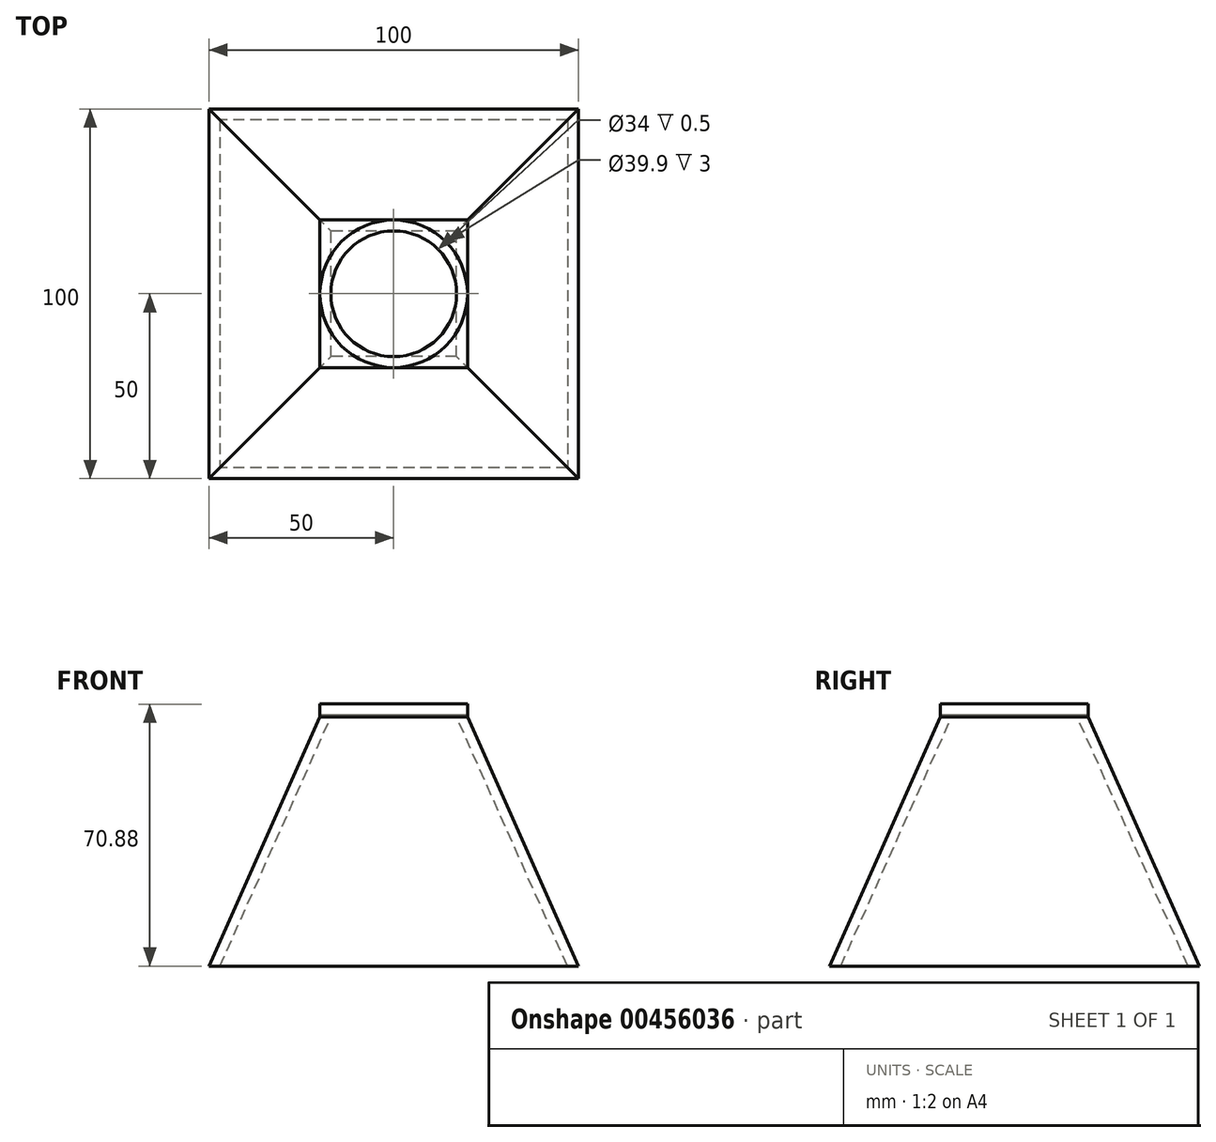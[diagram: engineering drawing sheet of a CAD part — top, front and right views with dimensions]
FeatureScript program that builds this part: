
annotation { "Feature Type Name" : "Feature", "Feature Type Description" : "" }
export const myFeature = defineFeature(function(context is Context, id is Id, definition is map)
    precondition{}
    {
        {
            var Q0;
            Q0=qCreatedBy(makeId("Top.planeOp"),FACE);
            var sketch = newSketch(context, id + "F0", { "sketchPlane" : qUnion([Q0])});
            skLineSegment(sketch, "E0.bottom", {"start": v(50, 50) * mm, "end": v(-50, 50) * mm});
            skLineSegment(sketch, "E0.top", {"start": v(50, -50) * mm, "end": v(-50, -50) * mm});
            skLineSegment(sketch, "E0.left", {"start": v(50, 50) * mm, "end": v(50, -50) * mm});
            skLineSegment(sketch, "E0.right", {"start": v(-50, 50) * mm, "end": v(-50, -50) * mm});
            skPoint(sketch, "E0.middle", {"position": v(0, 0) * mm});
            skLineSegment(sketch, "E1.0", {"start": v(47, -47) * mm, "end": v(-47, -47) * mm, "construction": true});
            skLineSegment(sketch, "E1.1", {"start": v(47, 47) * mm, "end": v(47, -47) * mm, "construction": true});
            skLineSegment(sketch, "E1.2", {"start": v(47, 47) * mm, "end": v(-47, 47) * mm, "construction": true});
            skLineSegment(sketch, "E1.3", {"start": v(-47, 47) * mm, "end": v(-47, -47) * mm, "construction": true});
            skLineSegment(sketch, "E2", {"start": v(0, 50) * mm, "end": v(0, -50) * mm, "construction": true});
            skLineSegment(sketch, "E3", {"start": v(-50, 0) * mm, "end": v(50, 0) * mm, "construction": true});
            skSolve(sketch);
        }
        {
            var Q0;
            Q0=qCreatedBy(makeId("Front.planeOp"),FACE);
            var sketch = newSketch(context, id + "F1", { "sketchPlane" : qUnion([Q0])});
            skLineSegment(sketch, "E4.0", {"start": v(-50, 0) * mm, "end": v(50, 0) * mm, "construction": true});
            skPoint(sketch, "E5.0", {"position": v(47, 0) * mm});
            skLineSegment(sketch, "E6", {"start": v(47, 0) * mm, "end": v(17, 67.38) * mm});
            skPoint(sketch, "E7.0", {"position": v(0, 0) * mm});
            skLineSegment(sketch, "E8", {"start": v(0, 0) * mm, "end": v(0, 105.56) * mm, "construction": true});
            skLineSegment(sketch, "E9", {"start": v(0, 67.38) * mm, "end": v(17, 67.38) * mm, "construction": true});
            skSolve(sketch);
        }
        {
            var Q0;
            Q0=qCreatedBy(makeId("Right.planeOp"),FACE);
            var sketch = newSketch(context, id + "F2", { "sketchPlane" : qUnion([Q0])});
            skLineSegment(sketch, "E10.0", {"start": v(50, 0) * mm, "end": v(-50, 0) * mm, "construction": true});
            skPoint(sketch, "E11.0", {"position": v(47, 0) * mm});
            skLineSegment(sketch, "E12", {"start": v(47, 0) * mm, "end": v(17, 67.38) * mm});
            skLineSegment(sketch, "E13.0", {"start": v(0, 0) * mm, "end": v(0, 105.56) * mm, "construction": true});
            skLineSegment(sketch, "E14", {"start": v(0, 67.38) * mm, "end": v(17, 67.38) * mm, "construction": true});
            skSolve(sketch);
        }
        {
            var Q0;
            Q0=qCreatedBy(makeId("Top.planeOp"),FACE);
            var Q1;
            Q1=sQuery(id+"F1.wireOp",EDGE,"E9");
            cPlane(context, id + "F3", {"entities" : qUnion([Q0, Q1]), "cplaneType" : CPlaneType.LINE_ANGLE, "offset" : 63.5 * mm, "angle" : 0 * degree, "width" : 152.4 * mm, "height" : 152.4 * mm});
        }
        {
            var Q0;
            Q0=qCreatedBy(id+"F3.planeOp",FACE);
            var sketch = newSketch(context, id + "F4", { "sketchPlane" : qUnion([Q0])});
            skCircle(sketch, "E15", {"center": v(0, 0) * mm, "radius": 20 * mm, "construction": true});
            skCircle(sketch, "E16.0", {"center": v(0, 0) * mm, "radius": 17 * mm, "construction": true});
            skLineSegment(sketch, "E17.bottom", {"start": v(20, 20) * mm, "end": v(-20, 20) * mm});
            skLineSegment(sketch, "E17.top", {"start": v(20, -20) * mm, "end": v(-20, -20) * mm});
            skLineSegment(sketch, "E17.left", {"start": v(20, 20) * mm, "end": v(20, -20) * mm});
            skLineSegment(sketch, "E17.right", {"start": v(-20, 20) * mm, "end": v(-20, -20) * mm});
            skPoint(sketch, "E18", {"position": v(0, -20) * mm});
            skPoint(sketch, "E19", {"position": v(20, 0) * mm});
            skLineSegment(sketch, "E20.0", {"start": v(17, -17) * mm, "end": v(-17, -17) * mm, "construction": true});
            skLineSegment(sketch, "E20.1", {"start": v(17, 17) * mm, "end": v(17, -17) * mm, "construction": true});
            skLineSegment(sketch, "E20.2", {"start": v(17, 17) * mm, "end": v(-17, 17) * mm, "construction": true});
            skLineSegment(sketch, "E20.3", {"start": v(-17, 17) * mm, "end": v(-17, -17) * mm, "construction": true});
            skSolve(sketch);
        }
        {
            var Q0;
            Q0=qCreatedBy(makeId("Front.planeOp"),FACE);
            var sketch = newSketch(context, id + "F5", { "sketchPlane" : qUnion([Q0])});
            skPoint(sketch, "E21.1", {"position": v(20, 67.38) * mm});
            skPoint(sketch, "E22.0", {"position": v(50, 0) * mm});
            skLineSegment(sketch, "E23", {"start": v(50, 0) * mm, "end": v(20, 67.38) * mm});
            skSolve(sketch);
        }
        {
            var Q0;
            Q0=qCreatedBy(makeId("Right.planeOp"),FACE);
            var sketch = newSketch(context, id + "F6", { "sketchPlane" : qUnion([Q0])});
            skPoint(sketch, "E24.0", {"position": v(50, 0) * mm});
            skPoint(sketch, "E25.0", {"position": v(20, 67.38) * mm});
            skLineSegment(sketch, "E26", {"start": v(50, 0) * mm, "end": v(20, 67.38) * mm});
            skSolve(sketch);
        }
        {
            var Q0;
            Q0=makeQuery(id+"F0.imprint","IMPRINT",FACE,{"disambiguationData":[TD([[makeQuery(id+"F0.imprint","IMPRINT",EDGE,{"derivedFrom":sQuery(id+"F0.wireOp",EDGE,"E0.bottom")}),1.0]])]});
            var Q1;
            Q1=makeQuery(id+"F4.imprint","IMPRINT",FACE,{"disambiguationData":[TD([[makeQuery(id+"F4.imprint","IMPRINT",EDGE,{"derivedFrom":sQuery(id+"F4.wireOp",EDGE,"E17.bottom")}),1.0]])]});
            var Q2;
            Q2=sQuery(id+"F5.wireOp",EDGE,"E23");
            var Q3;
            Q3=sQuery(id+"F6.wireOp",EDGE,"E26");
            loft(context, id + "F7", {"addGuides" : true, "sheetProfilesArray" : [{ "sheetProfileEntities" : qUnion([Q0]) }, { "sheetProfileEntities" : qUnion([Q1]) }], "guidesArray" : [{ "guideEntities" : qUnion([Q2]), "guideDerivativeType" : LoftGuideDerivativeType.DEFAULT, "guideDerivativeMagnitude" : 1 }, { "guideEntities" : qUnion([Q3]), "guideDerivativeType" : LoftGuideDerivativeType.DEFAULT, "guideDerivativeMagnitude" : 1 }]});
        }
        {
            var Q0;
            Q0=makeQuery(id+"F7.opLoft","CAP_FACE",FACE,{"disambiguationData":[OSD([makeQuery(id+"F0.imprint","IMPRINT",FACE,{"disambiguationData":[TD([[makeQuery(id+"F0.imprint","IMPRINT",EDGE,{"derivedFrom":sQuery(id+"F0.wireOp",EDGE,"E0.bottom")}),1.0]])]})])],"isStart":true});
            var sketch = newSketch(context, id + "F8", { "sketchPlane" : qUnion([Q0])});
            skLineSegment(sketch, "E27.0", {"start": v(47, 47) * mm, "end": v(-47, 47) * mm});
            skLineSegment(sketch, "E27.1", {"start": v(-47, -47) * mm, "end": v(-47, 47) * mm});
            skLineSegment(sketch, "E27.2", {"start": v(47, -47) * mm, "end": v(47, 47) * mm});
            skLineSegment(sketch, "E27.3", {"start": v(47, -47) * mm, "end": v(-47, -47) * mm});
            skSolve(sketch);
        }
        {
            var Q0;
            Q0=makeQuery(id+"F7.opLoft","CAP_FACE",FACE,{"disambiguationData":[OSD([makeQuery(id+"F4.imprint","IMPRINT",FACE,{"disambiguationData":[TD([[makeQuery(id+"F4.imprint","IMPRINT",EDGE,{"derivedFrom":sQuery(id+"F4.wireOp",EDGE,"E17.bottom")}),1.0]])]})])],"isStart":true});
            var sketch = newSketch(context, id + "F9", { "sketchPlane" : qUnion([Q0])});
            skLineSegment(sketch, "E28.1", {"start": v(-17, -17) * mm, "end": v(-17, 17) * mm});
            skLineSegment(sketch, "E28.2", {"start": v(17, 17) * mm, "end": v(-17, 17) * mm});
            skLineSegment(sketch, "E28.3", {"start": v(17, -17) * mm, "end": v(17, 17) * mm});
            skLineSegment(sketch, "E28.4", {"start": v(17, -17) * mm, "end": v(-17, -17) * mm});
            skSolve(sketch);
        }
        {
            var Q1;
            Q1 = qSketchRegion(id + "F8", true);
            var Q2;
            Q2 = qSketchRegion(id + "F9", true);
            loft(context, id + "F10", {"operationType" : NewBodyOperationType.REMOVE, "sheetProfilesArray" : [{ "sheetProfileEntities" : qUnion([Q1]) }, { "sheetProfileEntities" : qUnion([Q2]) }]});
        }
        {
            var Q0;
            Q0=makeQuery(id+"F4.imprint","IMPRINT",FACE,{"disambiguationData":[TD([[makeQuery(id+"F4.imprint","IMPRINT",EDGE,{"derivedFrom":sQuery(id+"F4.wireOp",EDGE,"E17.bottom")}),1.0]])]});
            var sketch = newSketch(context, id + "F11", { "sketchPlane" : qUnion([Q0])});
            skCircle(sketch, "E29.0", {"center": v(0, 0) * mm, "radius": 17 * mm});
            skLineSegment(sketch, "E30.1", {"start": v(-20, 20) * mm, "end": v(-20, -20) * mm});
            skLineSegment(sketch, "E30.2", {"start": v(20, -20) * mm, "end": v(-20, -20) * mm});
            skLineSegment(sketch, "E30.3", {"start": v(20, 20) * mm, "end": v(20, -20) * mm});
            skLineSegment(sketch, "E30.4", {"start": v(20, 20) * mm, "end": v(-20, 20) * mm});
            skSolve(sketch);
        }
        {
            var Q0;
            Q0 = qSketchRegion(id + "F11", true);
            extrude(context, id + "F12", {"entities" : qUnion([Q0]), "operationType" : NewBodyOperationType.ADD, "oppositeDirection" : true, "depth" : 3.5 * mm});
        }
        {
            var Q0;
            Q0=makeQuery(id+"F12.opExtrude","CAP_FACE",FACE,{"disambiguationData":[OSD([sQuery(id+"F11.wireOp",EDGE,"E29.0"),sQuery(id+"F11.wireOp",EDGE,"E30.1"),sQuery(id+"F11.wireOp",EDGE,"E30.2"),sQuery(id+"F11.wireOp",EDGE,"E30.3"),sQuery(id+"F11.wireOp",EDGE,"E30.4")])],"isStart":false});
            var sketch = newSketch(context, id + "F13", { "sketchPlane" : qUnion([Q0])});
            skCircle(sketch, "E31", {"center": v(0, 0) * mm, "radius": 19.95 * mm});
            skSolve(sketch);
        }
        {
            var Q0;
            Q0 = qSketchRegion(id + "F13", true);
            extrude(context, id + "F14", {"entities" : qUnion([Q0]), "operationType" : NewBodyOperationType.REMOVE, "oppositeDirection" : true, "depth" : 3 * mm});
        }
    });
